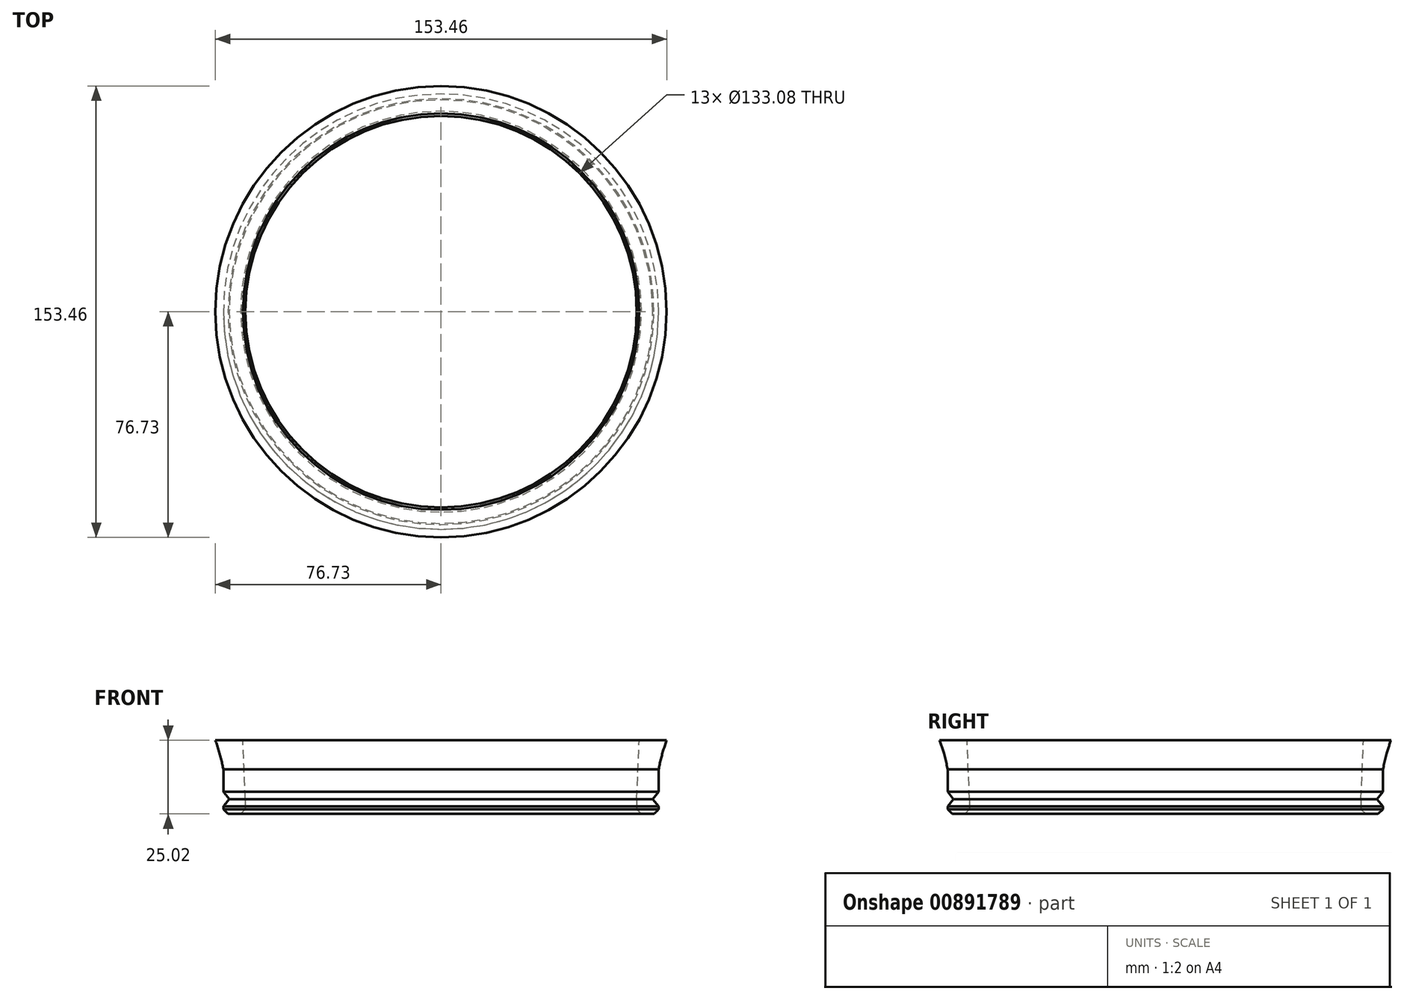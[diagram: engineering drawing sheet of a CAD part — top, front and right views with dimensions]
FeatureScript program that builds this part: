
annotation { "Feature Type Name" : "Feature", "Feature Type Description" : "" }
export const myFeature = defineFeature(function(context is Context, id is Id, definition is map)
    precondition{}
    {
        {
            var Q0;
            Q0=qCreatedBy(makeId("Front.planeOp"),FACE);
            var sketch = newSketch(context, id + "F0", { "sketchPlane" : qUnion([Q0])});
            skLineSegment(sketch, "E0", {"start": v(-74, 0) * mm, "end": v(-74, 0) * mm});
            skLineSegment(sketch, "E1", {"start": v(-74, 0) * mm, "end": v(-74, 2.55) * mm});
            skLineSegment(sketch, "E2", {"start": v(0, 0) * mm, "end": v(0, 61.52) * mm, "construction": true});
            skLineSegment(sketch, "E3.top", {"start": v(-67, 0) * mm, "end": v(-66.54, 0) * mm});
            skLineSegment(sketch, "E3.right", {"start": v(-66.54, 5) * mm, "end": v(-66.54, 0) * mm});
            skLineSegment(sketch, "E4.right", {"start": v(-66.54, 5) * mm, "end": v(-66.54, 5) * mm});
            skFitSpline(sketch, "E5", {"points": [v(-74, 15.1) * mm, v(-78.75, 29.58) * mm, v(-85.22, 36.5) * mm], "startDerivative": vector(-4.28, 24.7) * mm, "endDerivative": vector(-19.77, 12.2) * mm});
            skLineSegment(sketch, "E6", {"start": v(-67.38, 25.02) * mm, "end": v(-66.54, 5) * mm});
            skPoint(sketch, "E7.end.orphan", {"position": v(-69.93, 0) * mm});
            skLineSegment(sketch, "E8", {"start": v(-74, 0) * mm, "end": v(-67, 0) * mm});
            skLineSegment(sketch, "E9", {"start": v(-74, 7.55) * mm, "end": v(-72, 5.05) * mm});
            skLineSegment(sketch, "E10", {"start": v(-72, 5.05) * mm, "end": v(-74, 2.55) * mm});
            skLineSegment(sketch, "E11.trimOffspring", {"start": v(-74, 7.55) * mm, "end": v(-74, 15.1) * mm});
            skLineSegment(sketch, "E12", {"start": v(-76.73, 25.02) * mm, "end": v(-67.38, 25.02) * mm});
            skPoint(sketch, "E13.end.orphan", {"position": v(-68, 40) * mm});
            skSolve(sketch);
        }
        {
            var Q0;
            Q0=makeQuery(id+"F0.imprint","IMPRINT",FACE,{"disambiguationData":[TD([[makeQuery(id+"F0.imprint","IMPRINT",EDGE,{"derivedFrom":sQuery(id+"F0.wireOp",EDGE,"E1")}),-1.0]])]});
            var Q1;
            Q1=sQuery(id+"F0.wireOp",EDGE,"E2");
            revolve(context, id + "F1", {"surfaceOperationType" : NewSurfaceOperationType.NEW, "entities" : qUnion([Q0]), "axis" : qUnion([Q1]), "revolveType" : RevolveType.FULL});
        }
        {
            var Q0;
            Q0=makeQuery(id+"F1.opRevolve","SWEPT_FACE",FACE,{"disambiguationData":[OSD([sQuery(id+"F0.wireOp",EDGE,"E3.top"),sQuery(id+"F0.wireOp",EDGE,"E8")])]});
            var Q1;
            Q1=makeQuery(id+"F1.opRevolve","SWEPT_FACE",FACE,{"disambiguationData":[OSD([sQuery(id+"F0.wireOp",EDGE,"E13")])]});
            chamfer(context, id + "F2", {"entities" : qUnion([Q0, Q1]), "width" : 1.6 * mm, "tangentPropagation" : true});
        }
    });
